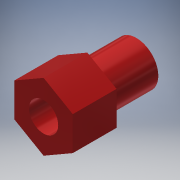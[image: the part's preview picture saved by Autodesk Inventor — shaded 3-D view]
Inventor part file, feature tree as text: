
AUTODESK INVENTOR PART (.ipt)
format: ipt  version: 2017 SP1 (Build 210196100, 196)  size: 131,072 bytes
history: native  units: in
note: dims shown in document units (in); Inventor stores cm internally (conversion verified against a paired STEP export)
features: extrude x2, sketch x2
ambient origin geometry x8: Origin, YZ Plane, XZ Plane, XY Plane, X Axis, Y Axis, Z Axis, Center Point
bodies: Solid1 (feature_tree)
feature tree (4):
  extrude  "Extrusion1"  Depth=0.375in
  extrude  "Extrusion2"  Depth=0.5in
  sketch  "Sketch1"  dims[d0=0.25in d1=0.375in]
  sketch  "Sketch2"  dims[d2=0.42in d3=0.0in d4=0.5in d5=0.375in d6=0.0in]
